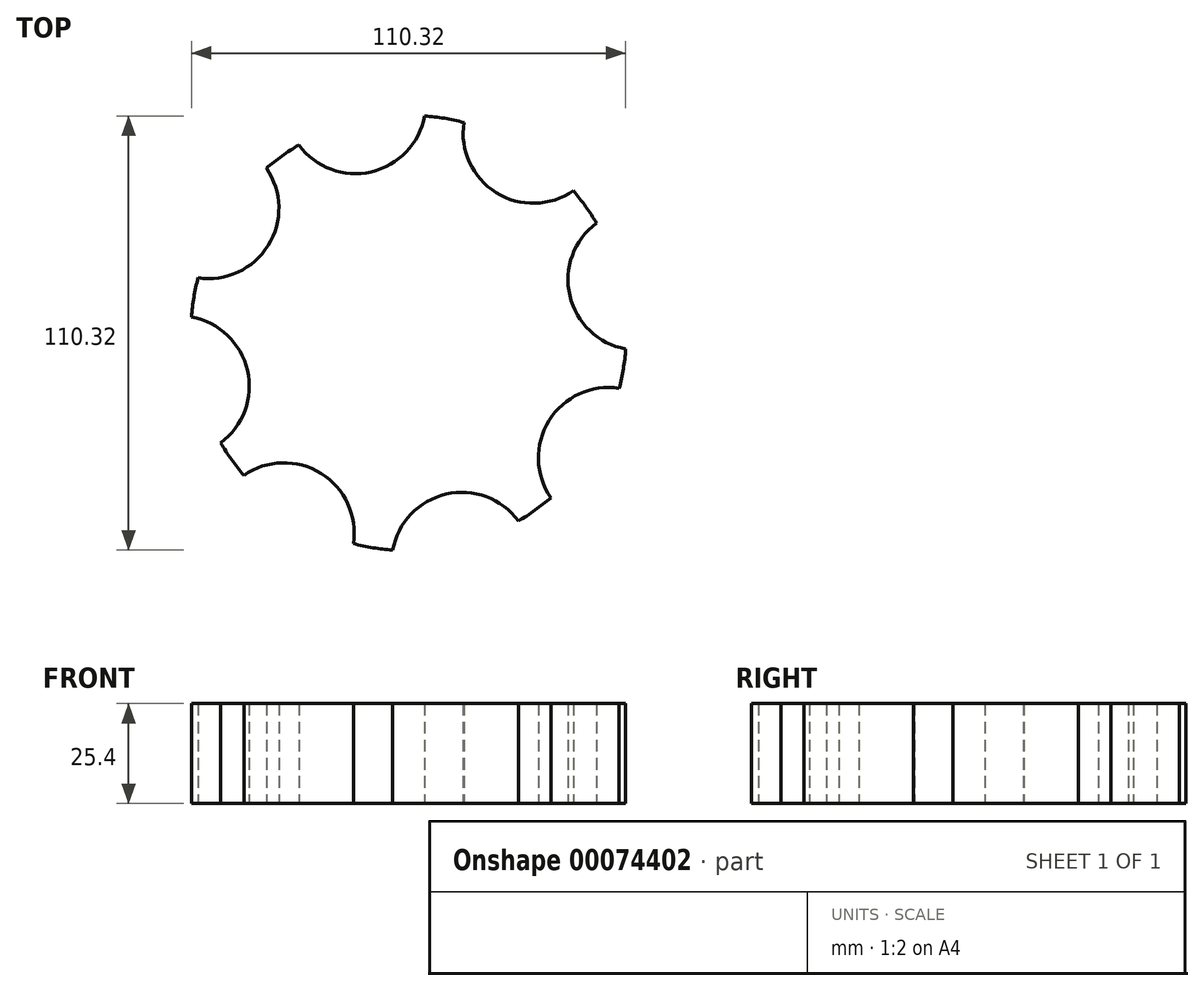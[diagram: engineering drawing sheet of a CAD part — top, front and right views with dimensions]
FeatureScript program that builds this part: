
annotation { "Feature Type Name" : "Feature", "Feature Type Description" : "" }
export const myFeature = defineFeature(function(context is Context, id is Id, definition is map)
    precondition{}
    {
        {
            var Q0;
            Q0=qCreatedBy(makeId("Top.planeOp"),FACE);
            var sketch = newSketch(context, id + "F0", { "sketchPlane" : qUnion([Q0])});
            skCircle(sketch, "E0", {"center": v(0, 0) * mm, "radius": 55.3 * mm});
            skSolve(sketch);
        }
        {
            var Q0;
            Q0 = qSketchRegion(id + "F0", true);
            extrude(context, id + "F1", {"entities" : qUnion([Q0]), "depth" : 25.4 * mm});
        }
        {
            var Q0;
            Q0=qCreatedBy(makeId("Top.planeOp"),FACE);
            var sketch = newSketch(context, id + "F2", { "sketchPlane" : qUnion([Q0])});
            skCircle(sketch, "E1", {"center": v(50.8, -31.68) * mm, "radius": 17.84 * mm});
            skSolve(sketch);
        }
        {
            var Q0;
            Q0=makeQuery(id+"F2.imprint","IMPRINT",FACE,{"disambiguationData":[TD([[makeQuery(id+"F2.imprint","IMPRINT",EDGE,{"derivedFrom":sQuery(id+"F2.wireOp",EDGE,"E1")}),1.0]])]});
            extrude(context, id + "F3", {"entities" : qUnion([Q0]), "depth" : 25.4 * mm});
        }
        {
            var Q0;
            Q0=makeQuery(id+"F3.opExtrude","SWEPT_BODY",BODY,{"disambiguationData":[OSD([sQuery(id+"F2.wireOp",EDGE,"E1")])]});
            var Q1;
            Q1=makeQuery(id+"F1.opExtrude","CAP_EDGE",EDGE,{"disambiguationData":[OSD([sQuery(id+"F0.wireOp",EDGE,"E0")])],"isStart":false});
            circularPattern(context, id + "F4", {"operationType" : NewBodyOperationType.REMOVE, "entities" : qUnion([Q0]), "axis" : qUnion([Q1]), "angle" : 360 * degree, "instanceCount" : 8, "equalSpace" : true});
        }
    });
